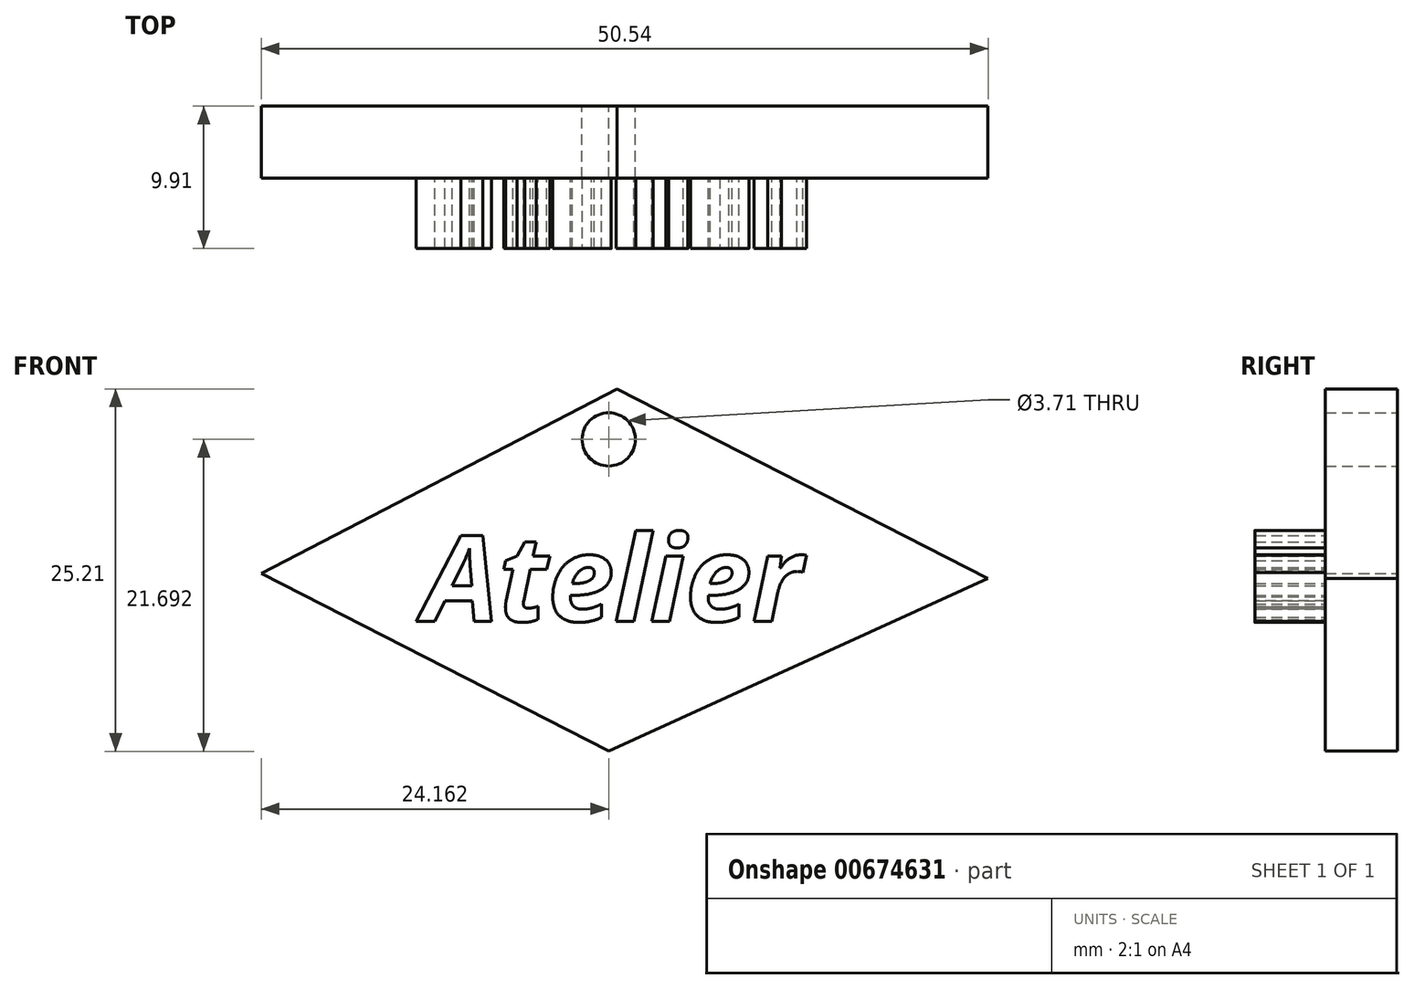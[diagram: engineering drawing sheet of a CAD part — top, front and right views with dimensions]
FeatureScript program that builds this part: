
annotation { "Feature Type Name" : "Feature", "Feature Type Description" : "" }
export const myFeature = defineFeature(function(context is Context, id is Id, definition is map)
    precondition{}
    {
        {
            var Q0;
            Q0=qCreatedBy(makeId("Front.planeOp"),FACE);
            var sketch = newSketch(context, id + "F0", { "sketchPlane" : qUnion([Q0])});
            skLineSegment(sketch, "E0", {"start": v(10.26, 31.8) * mm, "end": v(36.05, 18.61) * mm});
            skLineSegment(sketch, "E1", {"start": v(36.05, 18.61) * mm, "end": v(9.67, 6.6) * mm});
            skLineSegment(sketch, "E2", {"start": v(9.67, 6.6) * mm, "end": v(-14.49, 18.95) * mm});
            skLineSegment(sketch, "E3", {"start": v(-14.49, 18.95) * mm, "end": v(10.26, 31.8) * mm});
            skCircle(sketch, "E4", {"center": v(9.67, 28.28) * mm, "radius": 1.85 * mm});
            skSolve(sketch);
        }
        {
            var Q0;
            Q0 = qSketchRegion(id + "F0", true);
            extrude(context, id + "F1", {"entities" : qUnion([Q0]), "depth" : 5 * mm, "offsetDistance" : 25.4 * mm});
        }
        {
            var Q0;
            Q0=qCreatedBy(makeId("Front.planeOp"),FACE);
            var sketch = newSketch(context, id + "F2", { "sketchPlane" : qUnion([Q0])});
            skText(sketch, "E5", { "text": "Atelier", "fontName": "OpenSans-BoldItalic.ttf"});
            skPoint(sketch, "E6", {"position": v(-8.86, 18.9) * mm});
            skPoint(sketch, "E7", {"position": v(31.14, 18.9) * mm});
            const initialGuessF2  = {"E5": [-0.00322, 0.01563, 1, 0, 0.00599]};
            skSetInitialGuess(sketch, initialGuessF2);
            skSolve(sketch);
        }
        {
            var Q0;
            Q0 = qSketchRegion(id + "F2", true);
            extrude(context, id + "F3", {"entities" : qUnion([Q0]), "operationType" : NewBodyOperationType.ADD, "depth" : 9.9 * mm, "offsetDistance" : 25.4 * mm});
        }
    });
